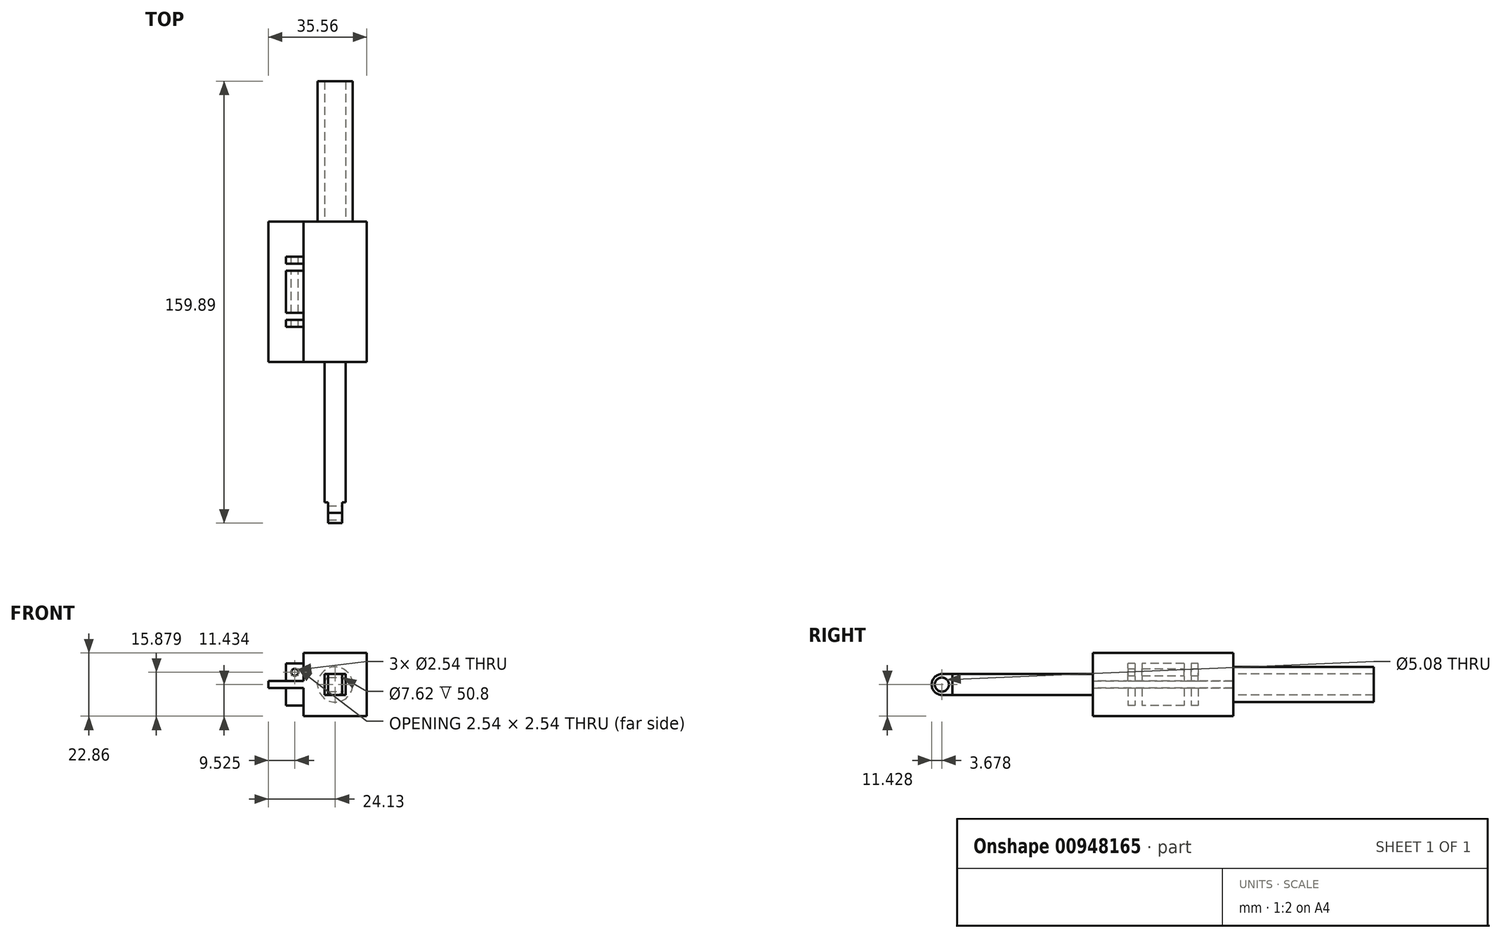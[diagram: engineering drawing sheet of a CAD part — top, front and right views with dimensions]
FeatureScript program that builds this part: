
annotation { "Feature Type Name" : "Feature", "Feature Type Description" : "" }
export const myFeature = defineFeature(function(context is Context, id is Id, definition is map)
    precondition{}
    {
        {
            var Q0;
            Q0=qCreatedBy(makeId("Right.planeOp"),FACE);
            var sketch = newSketch(context, id + "F0", { "sketchPlane" : qUnion([Q0])});
            skLineSegment(sketch, "E0.bottom", {"start": v(-52.43, 37.42) * mm, "end": v(-1.63, 37.42) * mm});
            skLineSegment(sketch, "E0.top", {"start": v(-52.43, 29.8) * mm, "end": v(-1.63, 29.8) * mm});
            skLineSegment(sketch, "E0.left", {"start": v(-52.43, 37.42) * mm, "end": v(-52.43, 29.8) * mm});
            skLineSegment(sketch, "E0.right", {"start": v(-1.63, 37.42) * mm, "end": v(-1.63, 29.8) * mm});
            skSolve(sketch);
        }
        {
            var Q0;
            Q0=makeQuery(id+"F0.imprint","IMPRINT",FACE,{"disambiguationData":[TD([[makeQuery(id+"F0.imprint","IMPRINT",EDGE,{"derivedFrom":sQuery(id+"F0.wireOp",EDGE,"E0.bottom")}),-1.0]])]});
            extrude(context, id + "F1", {"entities" : qUnion([Q0]), "depth" : 7.62 * mm, "offsetDistance" : 25.4 * mm});
        }
        {
            var Q0;
            Q0=makeQuery(id+"F1.opExtrude","SWEPT_FACE",FACE,{"disambiguationData":[OSD([sQuery(id+"F0.wireOp",EDGE,"E0.left")])]});
            var sketch = newSketch(context, id + "F2", { "sketchPlane" : qUnion([Q0])});
            skLineSegment(sketch, "E1.bottom", {"start": v(1.27, 37.42) * mm, "end": v(6.35, 37.42) * mm});
            skLineSegment(sketch, "E1.top", {"start": v(1.27, 29.8) * mm, "end": v(6.35, 29.8) * mm});
            skLineSegment(sketch, "E1.left", {"start": v(1.27, 37.42) * mm, "end": v(1.27, 29.8) * mm});
            skLineSegment(sketch, "E1.right", {"start": v(6.35, 37.42) * mm, "end": v(6.35, 29.8) * mm});
            skSolve(sketch);
        }
        {
            var Q0;
            Q0=makeQuery(id+"F2.imprint","IMPRINT",FACE,{"disambiguationData":[TD([[makeQuery(id+"F2.imprint","IMPRINT",EDGE,{"derivedFrom":sQuery(id+"F2.wireOp",EDGE,"E1.bottom")}),1.0]])]});
            extrude(context, id + "F3", {"entities" : qUnion([Q0]), "operationType" : NewBodyOperationType.ADD, "depth" : 7.62 * mm, "offsetDistance" : 25.4 * mm});
        }
        {
            var Q0;
            Q0=makeQuery(id+"F3.opExtrude","SWEPT_FACE",FACE,{"disambiguationData":[OSD([sQuery(id+"F2.wireOp",EDGE,"E1.right")])]});
            var sketch = newSketch(context, id + "F4", { "sketchPlane" : qUnion([Q0])});
            skCircle(sketch, "E2", {"center": v(-56.24, 33.6) * mm, "radius": 2.54 * mm});
            skPoint(sketch, "E2.centerSnap0", {"position": v(-60.05, 33.6) * mm});
            skArc(sketch, "E3", {"start": v(-56.24, 37.42) * mm, "mid": v(-59.92, 33.6) * mm, "end": v(-56.24, 29.8) * mm});
            skSolve(sketch);
        }
        {
            var Q0;
            Q0=makeQuery(id+"F4.imprint","IMPRINT",FACE,{"disambiguationData":[TD([[makeQuery(id+"F4.imprint","IMPRINT",EDGE,{"derivedFrom":sQuery(id+"F4.wireOp",EDGE,"E2")}),1.0]])]});
            var Q1;
            {var subQ0=sQuery(id+"F4.wireOp",EDGE,"E3");Q1=makeQuery(id+"F4.imprint","IMPRINT",FACE,{"disambiguationData":[TD([[makeQuery(id+"F4.imprint","IMPRINT",EDGE,{"derivedFrom":subQ0}),-1.0]])]});}
            extrude(context, id + "F5", {"entities" : qUnion([Q0, Q1]), "operationType" : NewBodyOperationType.REMOVE, "oppositeDirection" : true, "depth" : 25.4 * mm, "offsetDistance" : 25.4 * mm});
        }
        {
            var Q0;
            Q0=makeQuery(id+"F1.opExtrude","SWEPT_FACE",FACE,{"disambiguationData":[OSD([sQuery(id+"F0.wireOp",EDGE,"E0.right")])]});
            var sketch = newSketch(context, id + "F6", { "sketchPlane" : qUnion([Q0])});
            skLineSegment(sketch, "E4.bottom", {"start": v(7.62, 45.04) * mm, "end": v(-15.24, 45.04) * mm});
            skLineSegment(sketch, "E4.top", {"start": v(7.62, 22.18) * mm, "end": v(-15.24, 22.18) * mm});
            skLineSegment(sketch, "E4.left", {"start": v(7.62, 45.04) * mm, "end": v(7.62, 22.18) * mm});
            skLineSegment(sketch, "E4.right", {"start": v(-15.24, 45.04) * mm, "end": v(-15.24, 22.18) * mm});
            skPoint(sketch, "E4.middle", {"position": v(-3.81, 33.61) * mm});
            skPoint(sketch, "E4.middle.positionSnap0", {"position": v(-3.81, 37.42) * mm});
            skPoint(sketch, "E4.centerSnap0", {"position": v(-3.81, 37.42) * mm});
            skSolve(sketch);
        }
        {
            var Q0;
            Q0=makeQuery(id+"F6.imprint","IMPRINT",FACE,{"disambiguationData":[TD([[makeQuery(id+"F6.imprint","IMPRINT",EDGE,{"derivedFrom":sQuery(id+"F6.wireOp",EDGE,"E4.bottom")}),1.0]])]});
            var Q1;
            {var subQ0=sQuery(id+"F0.wireOp",EDGE,"E0.right");Q1=makeQuery(id+"F6.imprint","IMPRINT",FACE,{"disambiguationData":[TD([[makeQuery(id+"F6.imprint","IMPRINT",EDGE,{"derivedFrom":makeQuery(id+"F1.opExtrude","CAP_EDGE",EDGE,{"disambiguationData":[OSD([subQ0])],"isStart":true})}),-1.0]])]});}
            extrude(context, id + "F7", {"entities" : qUnion([Q0, Q1]), "operationType" : NewBodyOperationType.ADD, "depth" : 50.8 * mm, "offsetDistance" : 25.4 * mm});
        }
        {
            var Q0;
            Q0=makeQuery(id+"F7.opExtrude","CAP_FACE",FACE,{"disambiguationData":[OSD([sQuery(id+"F6.wireOp",EDGE,"E4.bottom"),sQuery(id+"F6.wireOp",EDGE,"E4.top"),sQuery(id+"F6.wireOp",EDGE,"E4.left"),sQuery(id+"F6.wireOp",EDGE,"E4.right")])],"isStart":false});
            var sketch = newSketch(context, id + "F8", { "sketchPlane" : qUnion([Q0])});
            skCircle(sketch, "E5", {"center": v(-3.81, 33.61) * mm, "radius": 3.81 * mm});
            skPoint(sketch, "E5.centerSnap0", {"position": v(-3.81, 45.04) * mm});
            skCircle(sketch, "E6", {"center": v(-3.81, 33.61) * mm, "radius": 6.35 * mm});
            skSolve(sketch);
        }
        {
            var Q0;
            Q0=makeQuery(id+"F8.imprint","IMPRINT",FACE,{"disambiguationData":[TD([[makeQuery(id+"F8.imprint","IMPRINT",EDGE,{"derivedFrom":sQuery(id+"F8.wireOp",EDGE,"E5")}),-1.0]])]});
            extrude(context, id + "F9", {"entities" : qUnion([Q0]), "operationType" : NewBodyOperationType.ADD, "depth" : 50.8 * mm, "offsetDistance" : 25.4 * mm});
        }
        {
            var Q0;
            Q0=makeQuery(id+"F7.opExtrude","SWEPT_FACE",FACE,{"disambiguationData":[OSD([sQuery(id+"F6.wireOp",EDGE,"E4.right")])]});
            var sketch = newSketch(context, id + "F10", { "sketchPlane" : qUnion([Q0])});
            skLineSegment(sketch, "E7.bottom", {"start": v(49.17, 34.88) * mm, "end": v(-1.63, 34.88) * mm});
            skLineSegment(sketch, "E7.top", {"start": v(49.17, 32.34) * mm, "end": v(-1.63, 32.34) * mm});
            skLineSegment(sketch, "E7.left", {"start": v(49.17, 34.88) * mm, "end": v(49.17, 32.34) * mm});
            skLineSegment(sketch, "E7.right", {"start": v(-1.63, 34.88) * mm, "end": v(-1.63, 32.34) * mm});
            skLineSegment(sketch, "E8", {"start": v(49.17, 34.88) * mm, "end": v(49.17, 45.04) * mm});
            skLineSegment(sketch, "E9", {"start": v(49.17, 32.34) * mm, "end": v(49.17, 22.18) * mm});
            skSolve(sketch);
        }
        {
            var Q0;
            Q0=makeQuery(id+"F10.imprint","IMPRINT",FACE,{"disambiguationData":[TD([[makeQuery(id+"F10.imprint","IMPRINT",EDGE,{"derivedFrom":sQuery(id+"F10.wireOp",EDGE,"E7.bottom")}),1.0]])]});
            extrude(context, id + "F11", {"entities" : qUnion([Q0]), "operationType" : NewBodyOperationType.ADD, "oppositeDirection" : true, "depth" : 35.56 * mm, "offsetDistance" : 25.4 * mm});
        }
        {
            var Q0;
            {var subQ1=sQuery(id+"F6.wireOp",EDGE,"E4.left");var subQ3=sQuery(id+"F6.wireOp",EDGE,"E4.bottom");Q0=makeQuery(id+"F11.boolean.opBoolean","SPLIT",FACE,{"disambiguationData":[TD([makeQuery(id+"F7.opExtrude","SWEPT_FACE",FACE,{"disambiguationData":[OSD([subQ3])]})])],"derivedFrom":makeQuery(id+"F7.opExtrude","SWEPT_FACE",FACE,{"disambiguationData":[OSD([subQ1])]})});}
            var sketch = newSketch(context, id + "F12", { "sketchPlane" : qUnion([Q0])});
            skLineSegment(sketch, "E10.bottom", {"start": v(-36.47, 34.88) * mm, "end": v(-11.07, 34.88) * mm});
            skLineSegment(sketch, "E10.top", {"start": v(-36.47, 41.23) * mm, "end": v(-11.07, 41.23) * mm});
            skLineSegment(sketch, "E10.left", {"start": v(-36.47, 34.88) * mm, "end": v(-36.47, 41.23) * mm});
            skLineSegment(sketch, "E10.right", {"start": v(-11.07, 34.88) * mm, "end": v(-11.07, 41.23) * mm});
            skLineSegment(sketch, "E11.bottom", {"start": v(-33.93, 41.23) * mm, "end": v(-31.39, 41.23) * mm});
            skLineSegment(sketch, "E11.top", {"start": v(-33.93, 34.88) * mm, "end": v(-31.39, 34.88) * mm});
            skLineSegment(sketch, "E11.left", {"start": v(-33.93, 41.23) * mm, "end": v(-33.93, 34.88) * mm});
            skLineSegment(sketch, "E11.right", {"start": v(-31.39, 41.23) * mm, "end": v(-31.39, 34.88) * mm});
            skLineSegment(sketch, "E12.bottom", {"start": v(-16.15, 41.23) * mm, "end": v(-13.6, 41.23) * mm});
            skLineSegment(sketch, "E12.top", {"start": v(-16.15, 34.88) * mm, "end": v(-13.6, 34.88) * mm});
            skLineSegment(sketch, "E12.left", {"start": v(-16.15, 41.23) * mm, "end": v(-16.15, 34.88) * mm});
            skLineSegment(sketch, "E12.right", {"start": v(-13.6, 41.23) * mm, "end": v(-13.6, 34.88) * mm});
            skSolve(sketch);
        }
        {
            var Q0;
            {var subQ0=sQuery(id+"F12.wireOp",EDGE,"E10.left");Q0=makeQuery(id+"F12.imprint","IMPRINT",FACE,{"disambiguationData":[TD([[makeQuery(id+"F12.imprint","IMPRINT",EDGE,{"derivedFrom":subQ0}),-1.0]])]});}
            var Q1;
            {var subQ0=sQuery(id+"F12.wireOp",EDGE,"E11.right");Q1=makeQuery(id+"F12.imprint","IMPRINT",FACE,{"disambiguationData":[TD([[makeQuery(id+"F12.imprint","IMPRINT",EDGE,{"derivedFrom":subQ0}),1.0]])]});}
            var Q2;
            {var subQ0=sQuery(id+"F12.wireOp",EDGE,"E10.right");Q2=makeQuery(id+"F12.imprint","IMPRINT",FACE,{"disambiguationData":[TD([[makeQuery(id+"F12.imprint","IMPRINT",EDGE,{"derivedFrom":subQ0}),1.0]])]});}
            extrude(context, id + "F13", {"entities" : qUnion([Q0, Q1, Q2]), "operationType" : NewBodyOperationType.ADD, "depth" : 6.35 * mm, "offsetDistance" : 25.4 * mm});
        }
        {
            var Q0;
            Q0=makeQuery(id+"F13.opExtrude","SWEPT_FACE",FACE,{"disambiguationData":[OSD([sQuery(id+"F12.wireOp",EDGE,"E10.left")])]});
            var sketch = newSketch(context, id + "F14", { "sketchPlane" : qUnion([Q0])});
            skCircle(sketch, "E13", {"center": v(10.8, 38.06) * mm, "radius": 1.27 * mm});
            skPoint(sketch, "E13.centerSnap0", {"position": v(10.8, 41.23) * mm});
            skSolve(sketch);
        }
        {
            var Q0;
            Q0=makeQuery(id+"F14.imprint","IMPRINT",FACE,{"disambiguationData":[TD([[makeQuery(id+"F14.imprint","IMPRINT",EDGE,{"derivedFrom":sQuery(id+"F14.wireOp",EDGE,"E13")}),1.0]])]});
            extrude(context, id + "F15", {"entities" : qUnion([Q0]), "operationType" : NewBodyOperationType.REMOVE, "oppositeDirection" : true, "depth" : 25.4 * mm, "offsetDistance" : 25.4 * mm});
        }
        {
            var Q0;
            {var subQ0=sQuery(id+"F6.wireOp",EDGE,"E4.top");var subQ2=sQuery(id+"F6.wireOp",EDGE,"E4.left");Q0=makeQuery(id+"F11.boolean.opBoolean","SPLIT",FACE,{"disambiguationData":[TD([makeQuery(id+"F7.opExtrude","SWEPT_FACE",FACE,{"disambiguationData":[OSD([subQ0])]})])],"derivedFrom":makeQuery(id+"F7.opExtrude","SWEPT_FACE",FACE,{"disambiguationData":[OSD([subQ2])]})});}
            var sketch = newSketch(context, id + "F16", { "sketchPlane" : qUnion([Q0])});
            skLineSegment(sketch, "E14.bottom", {"start": v(-36.47, 32.34) * mm, "end": v(-11.07, 32.34) * mm});
            skLineSegment(sketch, "E14.top", {"start": v(-36.47, 26) * mm, "end": v(-11.07, 26) * mm});
            skLineSegment(sketch, "E14.left", {"start": v(-36.47, 32.34) * mm, "end": v(-36.47, 26) * mm});
            skLineSegment(sketch, "E14.right", {"start": v(-11.07, 32.34) * mm, "end": v(-11.07, 26) * mm});
            skLineSegment(sketch, "E15.bottom", {"start": v(-33.93, 32.34) * mm, "end": v(-31.39, 32.34) * mm});
            skLineSegment(sketch, "E15.top", {"start": v(-33.93, 26) * mm, "end": v(-31.39, 26) * mm});
            skLineSegment(sketch, "E15.left", {"start": v(-33.93, 32.34) * mm, "end": v(-33.93, 26) * mm});
            skLineSegment(sketch, "E15.right", {"start": v(-31.39, 32.34) * mm, "end": v(-31.39, 26) * mm});
            skLineSegment(sketch, "E16.bottom", {"start": v(-16.15, 32.34) * mm, "end": v(-13.6, 32.34) * mm});
            skLineSegment(sketch, "E16.top", {"start": v(-16.15, 26) * mm, "end": v(-13.6, 26) * mm});
            skLineSegment(sketch, "E16.left", {"start": v(-16.15, 32.34) * mm, "end": v(-16.15, 26) * mm});
            skLineSegment(sketch, "E16.right", {"start": v(-13.6, 32.34) * mm, "end": v(-13.6, 26) * mm});
            skSolve(sketch);
        }
        {
            var Q0;
            {var subQ0=sQuery(id+"F16.wireOp",EDGE,"E14.left");Q0=makeQuery(id+"F16.imprint","IMPRINT",FACE,{"disambiguationData":[TD([[makeQuery(id+"F16.imprint","IMPRINT",EDGE,{"derivedFrom":subQ0}),1.0]])]});}
            var Q1;
            {var subQ0=sQuery(id+"F16.wireOp",EDGE,"E15.right");Q1=makeQuery(id+"F16.imprint","IMPRINT",FACE,{"disambiguationData":[TD([[makeQuery(id+"F16.imprint","IMPRINT",EDGE,{"derivedFrom":subQ0}),1.0]])]});}
            var Q2;
            {var subQ0=sQuery(id+"F16.wireOp",EDGE,"E14.right");Q2=makeQuery(id+"F16.imprint","IMPRINT",FACE,{"disambiguationData":[TD([[makeQuery(id+"F16.imprint","IMPRINT",EDGE,{"derivedFrom":subQ0}),-1.0]])]});}
            extrude(context, id + "F17", {"entities" : qUnion([Q0, Q1, Q2]), "operationType" : NewBodyOperationType.ADD, "depth" : 6.35 * mm, "offsetDistance" : 25.4 * mm});
        }
    });
